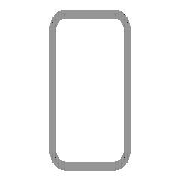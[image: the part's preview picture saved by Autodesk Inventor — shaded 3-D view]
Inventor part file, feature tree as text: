
AUTODESK INVENTOR PART (.ipt)
format: ipt  version: 2025 (Build 290162010, 162A)  size: 133,120 bytes
history: native  units: mm (DEFAULTED — no unit token found)
features: other x4, sketch x1, plane x1
ambient origin geometry x8: Origin, YZ Plane, XZ Plane, XY Plane, X Axis, Y Axis, Z Axis, Center Point
bodies: Solid1 (feature_tree), Body (feature_tree)
feature tree (6):
  parser-record x1  (decoder bookkeeping rows leaked as tree rows — omitted from the tree; the rows remain in map.json)
  other  "Driven Length"
  other  "Start Plane"
  other  "End Plane"
  sketch  "Sketch3"  dims[d3=1120.0mm d4=0.0mm d7=6.0mm d9=40.0mm d11=60.0mm d12=3.0mm d13=-0.0mm d14=1120.0mm d15=20.0mm d16=30.0mm d17=90.0deg d18=1120.0mm]
  plane  "Work Plane3"
